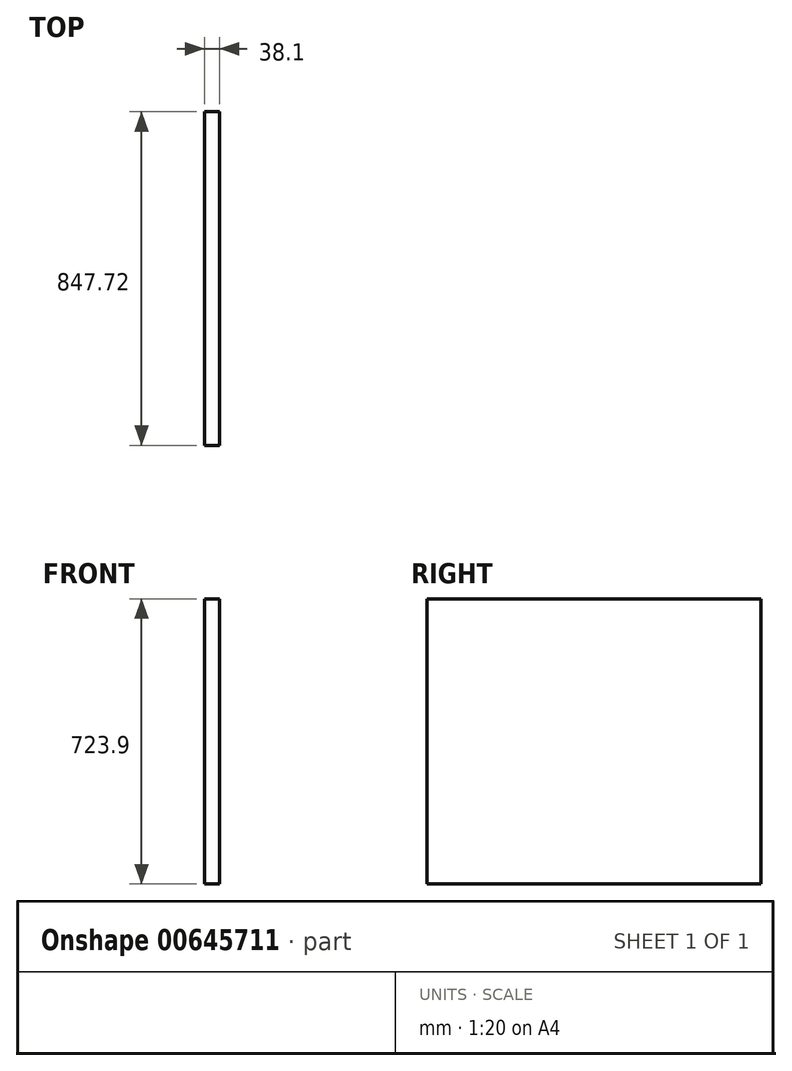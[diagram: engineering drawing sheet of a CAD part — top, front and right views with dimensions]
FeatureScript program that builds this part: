
annotation { "Feature Type Name" : "Feature", "Feature Type Description" : "" }
export const myFeature = defineFeature(function(context is Context, id is Id, definition is map)
    precondition{}
    {
        {
            var Q0;
            Q0=qCreatedBy(makeId("Right.planeOp"),FACE);
            var sketch = newSketch(context, id + "F0", { "sketchPlane" : qUnion([Q0])});
            skLineSegment(sketch, "E0.bottom", {"start": v(423.86, 361.95) * mm, "end": v(-423.86, 361.95) * mm});
            skLineSegment(sketch, "E0.top", {"start": v(423.86, -361.95) * mm, "end": v(-423.86, -361.95) * mm});
            skLineSegment(sketch, "E0.left", {"start": v(423.86, 361.95) * mm, "end": v(423.86, -361.95) * mm});
            skLineSegment(sketch, "E0.right", {"start": v(-423.86, 361.95) * mm, "end": v(-423.86, -361.95) * mm});
            skPoint(sketch, "E0.middle", {"position": v(0, 0) * mm});
            skSolve(sketch);
        }
        {
            var Q0;
            Q0=makeQuery(id+"F0.imprint","IMPRINT",FACE,{"disambiguationData":[TD([[makeQuery(id+"F0.imprint","IMPRINT",EDGE,{"derivedFrom":sQuery(id+"F0.wireOp",EDGE,"E0.bottom")}),1.0]])]});
            extrude(context, id + "F1", {"entities" : qUnion([Q0]), "depth" : 38.1 * mm, "offsetDistance" : 25.4 * mm});
        }
    });
